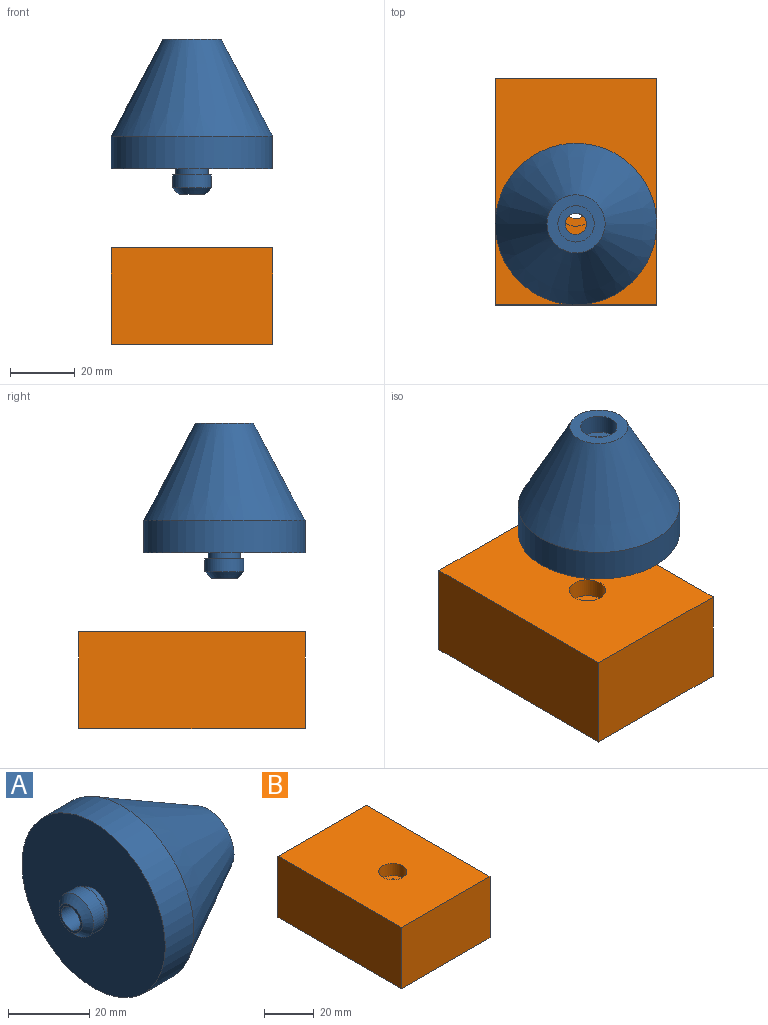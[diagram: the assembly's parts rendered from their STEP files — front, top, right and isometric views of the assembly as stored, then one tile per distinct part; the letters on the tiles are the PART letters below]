
ASSEMBLY  parts=2 mates=1
PART A: 12 faces, bbox 48x50x50 mm
  f0: plane 18x18mm, normal (1,0,0), area 155.1mm2, adj f1,f11
  f1: cone r=9mm half-angle=28.1deg, axis (-1,0,0), area 3631.7mm2, adj f0,f2
  f2: cylinder r=25mm len=50mm, axis (-1,0,0), area 1570.8mm2, adj f1,f3
  f3: plane 50x50mm, normal (-1,0,0), area 1885mm2, adj f2,f4
  f4: cylinder r=5mm len=10mm, axis (-1,0,0), area 62.8mm2, adj f3,f5
  f5: plane 12x12mm, normal (1,0,0), area 34.6mm2, adj f4,f6
  f6: cylinder r=6mm len=12mm, axis (-1,0,0), area 150.8mm2, adj f5,f7
  f7: cone r=6mm half-angle=45deg, axis (1,0,0), area 88.9mm2, adj f6,f8
  f8: plane 8x8mm, normal (-1,0,0), area 16.1mm2, adj f7,f9
  f9: cylinder r=3.3mm len=42mm, axis (1,0,0), area 870.8mm2, adj f8,f10
  f10: plane 11.25x11.25mm, normal (1,0,0), area 65.2mm2, adj f9,f11
  f11: cylinder r=5.62mm len=11.25mm, axis (1,0,0), area 212.1mm2, adj f0,f10
PART B: 11 faces, bbox 50x70x30 mm
  f0: cylinder r=5mm len=10mm, axis (0,0,-1), area 246.9mm2, adj f4,f7,f8
  f1: plane 70x30mm, normal (1,0,0), area 2100mm2, adj f2,f4,f5,f6
  f2: plane 70x50mm, normal (0,0,1), area 3400.6mm2, adj f1,f3,f5,f6,f10
  f3: plane 70x30mm, normal (-1,0,0), area 2100mm2, adj f2,f4,f5,f6
  f4: plane 70x50mm, normal (0,0,-1), area 3401.9mm2, adj f0,f1,f3,f5,f6,f8
  f5: plane 50x30mm, normal (0,-1,0), area 1500mm2, adj f1,f2,f3,f4
  f6: plane 50x30mm, normal (0,1,0), area 1500mm2, adj f1,f2,f3,f4
  f7: plane 10x8.91mm, normal (0,0,-1), area 63.9mm2, adj f0,f8
  f8: cylinder r=3.3mm len=24mm, axis (0,0,1), area 416.2mm2, adj f0,f4,f7,f9
  f9: plane 11.25x11.25mm, normal (0,0,1), area 65.2mm2, adj f8,f10
  f10: cylinder r=5.62mm len=11.25mm, axis (0,0,1), area 212.1mm2, adj f2,f9
PLACE A rot(axis=(-0.12,-0.99,-0.12),90.9deg) t=(105.87,628.55,91.7)mm
PLACE B t=(105.87,673.55,52.18)mm fixed
MATE cylindrical A.f1 <-> B.f0  axis (0,0,-1) through (105.87,628.55,83.7)mm
